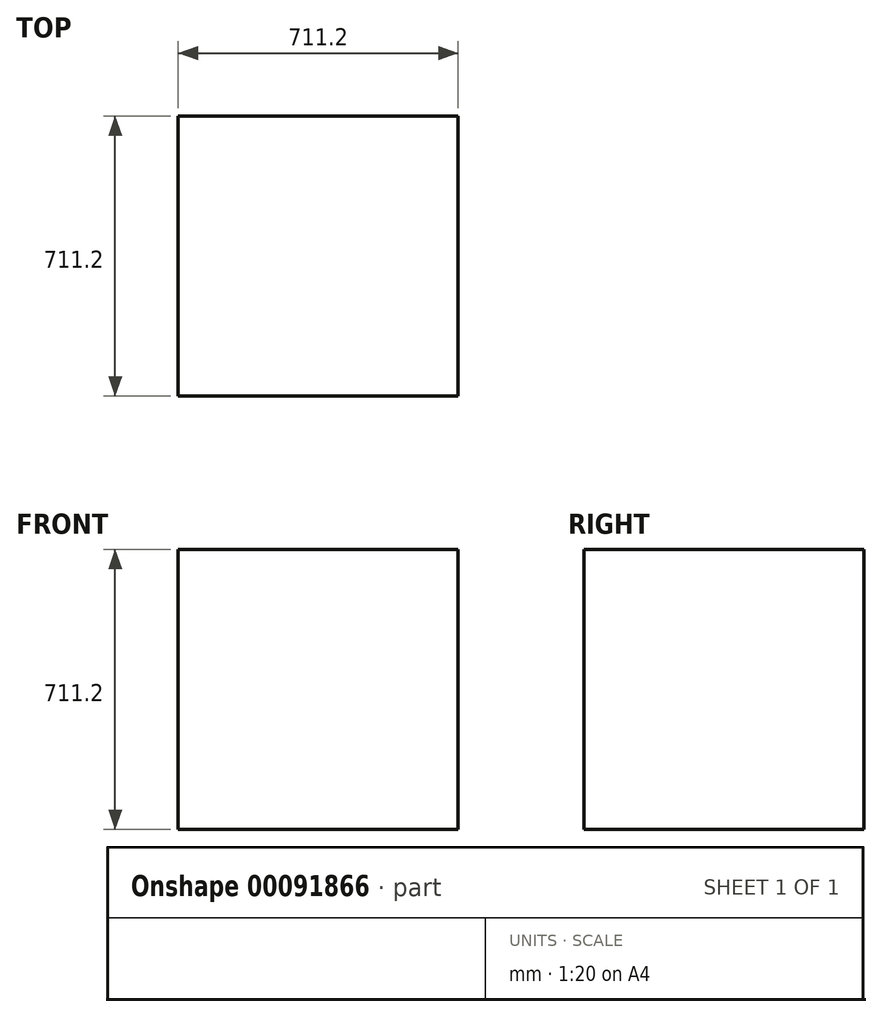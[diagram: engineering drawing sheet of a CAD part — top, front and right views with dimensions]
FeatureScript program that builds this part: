
annotation { "Feature Type Name" : "Feature", "Feature Type Description" : "" }
export const myFeature = defineFeature(function(context is Context, id is Id, definition is map)
    precondition{}
    {
        {
            var Q0;
            Q0=qCreatedBy(makeId("Top.planeOp"),FACE);
            var sketch = newSketch(context, id + "F1", { "sketchPlane" : qUnion([Q0])});
            skLineSegment(sketch, "E0.bottom", {"start": v(355.6, 355.6) * mm, "end": v(-355.6, 355.6) * mm});
            skLineSegment(sketch, "E0.top", {"start": v(355.6, -355.6) * mm, "end": v(-355.6, -355.6) * mm});
            skLineSegment(sketch, "E0.left", {"start": v(355.6, 355.6) * mm, "end": v(355.6, -355.6) * mm});
            skLineSegment(sketch, "E0.right", {"start": v(-355.6, 355.6) * mm, "end": v(-355.6, -355.6) * mm});
            skPoint(sketch, "E0.middle", {"position": v(0, 0) * mm});
            skSolve(sketch);
        }
        {
            var Q0;
            Q0 = qSketchRegion(id + "F1", true);
            extrude(context, id + "F2", {"entities" : qUnion([Q0]), "endBound" : BoundingType.SYMMETRIC, "depth" : 711.2 * mm});
        }
    });
